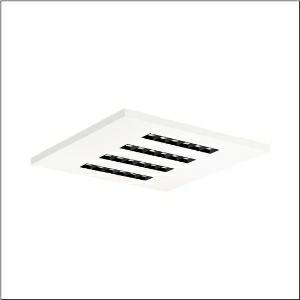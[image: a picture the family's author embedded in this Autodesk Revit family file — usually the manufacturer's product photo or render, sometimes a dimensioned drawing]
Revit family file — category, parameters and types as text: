
# Revit family: silica_r__21_square_51mx6kdu44w_ebd5
name_source: partatom
category: Lighting Fixtures
units: mm (PartAtom-declared; Revit-internal decimal feet)

## family parameters
Cut with Voids When Loaded = No
Host = Face
Light Source = No
Part Type = Normal
Room Calculation Point = No
Round Connector Dimension = Use Diameter
Shared = No

## types (1)
- --- (1 x LED, 4600 lm, 29.6 W, 4000K)
    Apparent Load = 30 VA
    CIE Flux Codes = 86 100 100 100 100
    Color Rendering = 80
    Color Temperature = 4000K
    Default Elevation = 1800 mm
    Description = Silica® 21 Square, office luminaire, primary light control with lens, of PMMA, primary anti-glare with reflector, of PC, black, CAT 2 (L<= 3000cd/m²), light emission: direct distribution, primary light characteristic: symmetric, installation type: lay-in mounting, LED, rated luminous flux: 4.600lm, luminous efficacy: 155lm/W, light colour: 840, colour temperature: 4000K, control gear: DALI 2, with terminal, 5-pole, mains connection: 220..240V, AC, 50/60Hz, rated input power: 29.6W, luminaire housing, of sheet steel, coated, traffic white (RAL 9016), module: M625, length: 622mm, width: 622mm, height: 33mm, protection rating (complete): IP20, insulation class (complete): insulation class I (protective earthing), certification: CE, ENEC, VDE, permissible operating ambient temperature: -20..+40°C, standard: EN 50419, packaging unit: 1 piece
    Height = 0 mm  [stored 0 ft]
    Lamp = 1 x LED
    Lamp Light Flux = 4600 lm
    Lamp Power = 29.6 W
    Lamp count = 1
    Length = 622 mm
    Luminous efficacy = 155 lm/W
    Manufacturer = Siteco
    ModVariant = No
    Model = 51MX6KDU44W
    Mounting Place = Ceiling
    Mounting Type = Recessed
    Number of Poles = 1
    OnlyDefault = Yes
    Power Factor = 1
    Product Name = Silica® 21 Square
    Product group = office luminaire | ceiling recessed
    ProductGroupID = 401
    Protection Class = Protection class I
    Protection Degree = IP 20
    RLX_Detail_Level = 1
    RLX_Emergency_Light_Flux = 0 lm
    RLX_Emergency_Type = 0
    RLX_Emergency_Type_DB = No
    RlxData = <blob elided: 21205 chars, md5=3c3c0a0c>
    Socket = socket
    Standby Power = 0 W
    System Light Flux = 4600 lm
    System Power = 30 W
    Type Comments = factory setting: luminous flux: 100 % | dim-lin: 254 | 399 mA
    Type Image = l_1275207.jpg
    URL = http://relux.com
    VarID = @adj_083950
    Voltage = 0 V
    Weight = 0.00 kg
    Width = 622 mm

note: [stored X ft] marks values corroborated as IEEE doubles in the binary element streams (Revit-internal decimal feet)

## geometry (parser evidence)
native form markers: Blend x4, Sweep x12
no freeform markers — native parametric forms only
